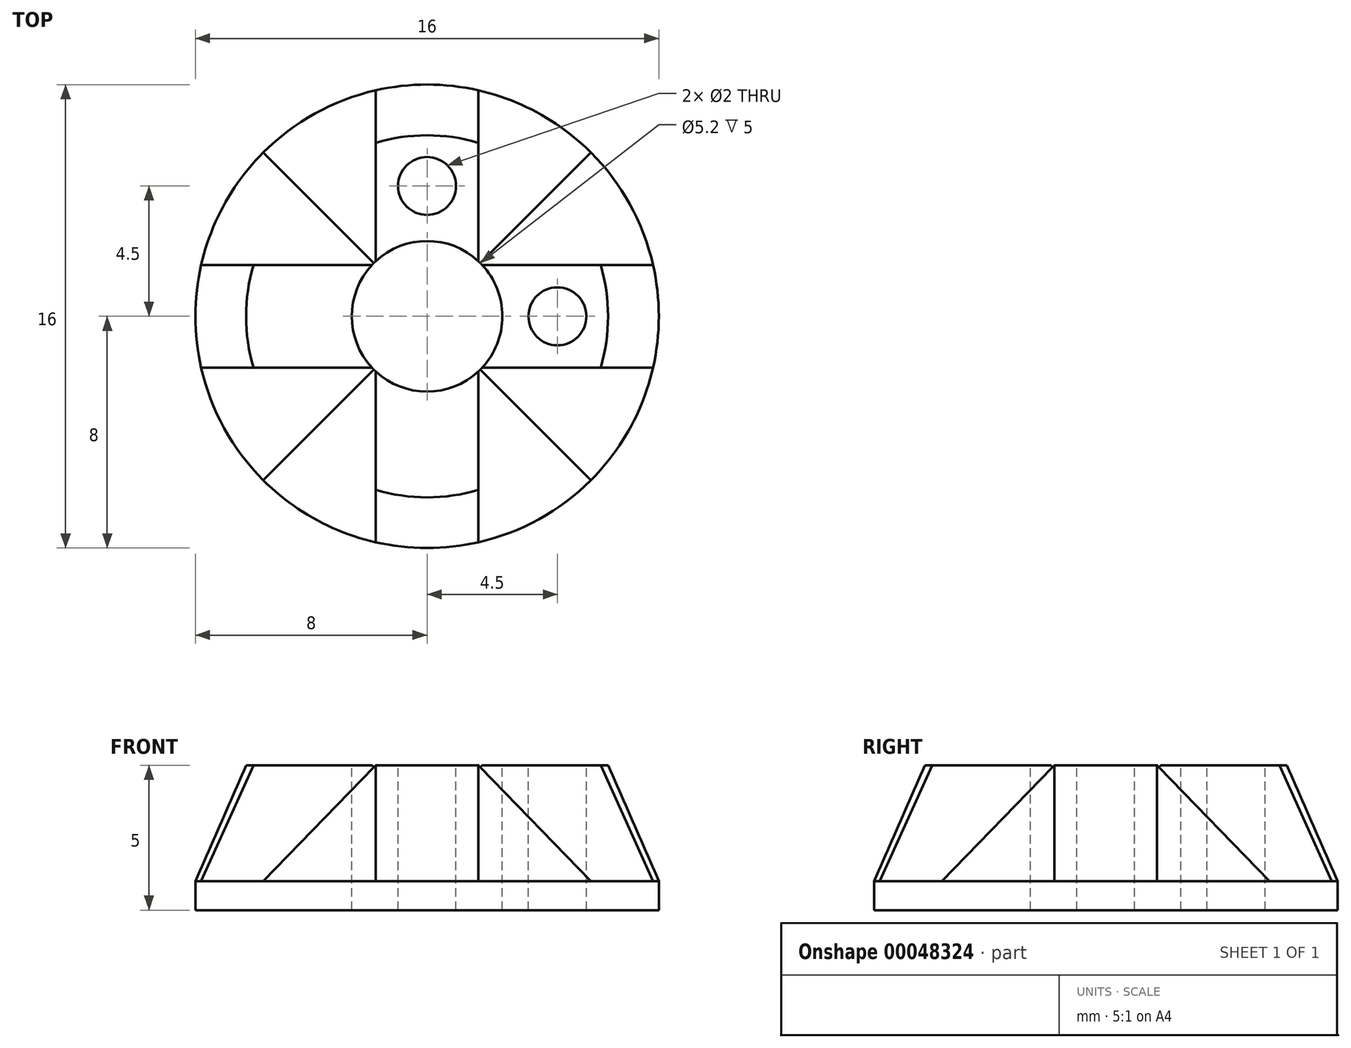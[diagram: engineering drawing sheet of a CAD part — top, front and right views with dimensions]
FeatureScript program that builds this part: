
annotation { "Feature Type Name" : "Feature", "Feature Type Description" : "" }
export const myFeature = defineFeature(function(context is Context, id is Id, definition is map)
    precondition{}
    {
        {
            var Q0;
            Q0=qCreatedBy(makeId("Top.planeOp"),FACE);
            var sketch = newSketch(context, id + "F0", { "sketchPlane" : qUnion([Q0])});
            skLineSegment(sketch, "E0", {"start": v(0, 0) * mm, "end": v(0, 6.25) * mm, "construction": true});
            skLineSegment(sketch, "E1", {"start": v(0, 6.25) * mm, "end": v(1.77, 6.25) * mm, "construction": true});
            skLineSegment(sketch, "E2.left", {"start": v(1.77, 6) * mm, "end": v(1.77, 1.78) * mm});
            skLineSegment(sketch, "E2.right", {"start": v(-1.78, 6) * mm, "end": v(-1.78, 1.77) * mm});
            skLineSegment(sketch, "E3", {"start": v(0, 0) * mm, "end": v(6.63, 6.63) * mm, "construction": true});
            skLineSegment(sketch, "E4.MirrorCS", {"start": v(6, 1.78) * mm, "end": v(1.78, 1.78) * mm});
            skLineSegment(sketch, "E5.MirrorCS", {"start": v(6, -1.78) * mm, "end": v(1.78, -1.78) * mm});
            skLineSegment(sketch, "E6", {"start": v(0, 0) * mm, "end": v(0, 4.5) * mm, "construction": true});
            skLineSegment(sketch, "E7", {"start": v(0, 4.5) * mm, "end": v(0, -4.5) * mm, "construction": true});
            skPoint(sketch, "E7.endSnap0", {"position": v(0, -1.78) * mm});
            skArc(sketch, "E8", {"start": v(6, -1.77) * mm, "mid": v(6.25, 0) * mm, "end": v(6, 1.78) * mm});
            skPoint(sketch, "E9.orphan", {"position": v(-1.78, 6.25) * mm});
            skPoint(sketch, "E10.orphan", {"position": v(6.25, 1.78) * mm});
            skPoint(sketch, "E11.MirrorCS.end.orphan", {"position": v(6.25, -1.78) * mm});
            skPoint(sketch, "E12.orphan", {"position": v(1.77, -6.25) * mm});
            skPoint(sketch, "E13.orphan", {"position": v(-6.25, -1.78) * mm});
            skPoint(sketch, "E14.MirrorCS.start.orphan", {"position": v(-6.25, 1.78) * mm});
            skPoint(sketch, "E15.orphan", {"position": v(-6.25, 1.77) * mm});
            skArc(sketch, "E16.trimOffspring", {"start": v(-1.77, -6) * mm, "mid": v(0, -6.25) * mm, "end": v(1.77, -6) * mm});
            skArc(sketch, "E17.trimOffspring", {"start": v(-6, 1.77) * mm, "mid": v(-6.25, 0) * mm, "end": v(-6, -1.77) * mm});
            skArc(sketch, "E18.trimOffspring", {"start": v(1.78, 6) * mm, "mid": v(0, 6.25) * mm, "end": v(-1.78, 6) * mm});
            skPoint(sketch, "E19.orphan", {"position": v(-1.77, -6.25) * mm});
            skLineSegment(sketch, "E20.trimOffspring", {"start": v(-1.78, -1.78) * mm, "end": v(-1.77, -6) * mm});
            skLineSegment(sketch, "E21.trimOffspring", {"start": v(-1.78, -1.78) * mm, "end": v(-6, -1.78) * mm});
            skLineSegment(sketch, "E22.trimOffspring", {"start": v(-1.78, 1.77) * mm, "end": v(-6, 1.77) * mm});
            skLineSegment(sketch, "E23", {"start": v(-1.78, 1.77) * mm, "end": v(1.78, -1.78) * mm});
            skLineSegment(sketch, "E24", {"start": v(1.78, 1.78) * mm, "end": v(-1.78, -1.78) * mm});
            skLineSegment(sketch, "E25.trimOffspring", {"start": v(1.77, -1.78) * mm, "end": v(1.77, -6) * mm});
            skSolve(sketch);
        }
        {
            var Q0;
            Q0=qCreatedBy(makeId("Top.planeOp"),FACE);
            cPlane(context, id + "F1", {"entities" : qUnion([Q0]), "cplaneType" : CPlaneType.OFFSET, "offset" : 5 * mm, "oppositeDirection" : true, "width" : 150 * mm, "height" : 150 * mm});
        }
        {
            var Q0;
            Q0=qCreatedBy(id+"F1.planeOp",FACE);
            var sketch = newSketch(context, id + "F2", { "sketchPlane" : qUnion([Q0])});
            skPoint(sketch, "E26.0", {"position": v(0, 0) * mm});
            skCircle(sketch, "E27", {"center": v(0, 0) * mm, "radius": 8 * mm});
            skSolve(sketch);
        }
        {
            var Q0;
            Q0 = qSketchRegion(id + "F2", true);
            extrude(context, id + "F3", {"entities" : qUnion([Q0]), "depth" : 1 * mm});
        }
        {
            var Q0;
            Q0=makeQuery(id+"F3.opExtrude","CAP_FACE",FACE,{"disambiguationData":[OSD([sQuery(id+"F2.wireOp",EDGE,"E27")])],"isStart":false});
            var sketch = newSketch(context, id + "F4", { "sketchPlane" : qUnion([Q0])});
            skPoint(sketch, "E28.0", {"position": v(0, 0) * mm});
            skLineSegment(sketch, "E29", {"start": v(0, 0) * mm, "end": v(0, -8) * mm, "construction": true});
            skLineSegment(sketch, "E30", {"start": v(5.66, 5.66) * mm, "end": v(-5.66, -5.66) * mm});
            skLineSegment(sketch, "E31", {"start": v(-5.66, 5.66) * mm, "end": v(5.66, -5.66) * mm});
            skLineSegment(sketch, "E32.0", {"start": v(-1.78, -1.78) * mm, "end": v(-7.8, -1.78) * mm, "construction": true});
            skLineSegment(sketch, "E33.0", {"start": v(-1.78, 1.77) * mm, "end": v(-7.8, 1.77) * mm, "construction": true});
            skLineSegment(sketch, "E34.0", {"start": v(-1.78, 7.8) * mm, "end": v(-1.78, 1.77) * mm, "construction": true});
            skLineSegment(sketch, "E35.0", {"start": v(7.8, 1.78) * mm, "end": v(1.78, 1.78) * mm, "construction": true});
            skLineSegment(sketch, "E36.0", {"start": v(7.8, -1.78) * mm, "end": v(1.78, -1.78) * mm, "construction": true});
            skPoint(sketch, "E37.orphan", {"position": v(-6, -1.78) * mm});
            skPoint(sketch, "E38.orphan", {"position": v(-6, 1.77) * mm});
            skPoint(sketch, "E39.orphan", {"position": v(-1.78, 6) * mm});
            skLineSegment(sketch, "E40.0", {"start": v(1.77, 7.8) * mm, "end": v(1.77, 1.78) * mm, "construction": true});
            skLineSegment(sketch, "E41.0", {"start": v(1.77, -1.78) * mm, "end": v(1.77, -7.8) * mm, "construction": true});
            skLineSegment(sketch, "E42.0", {"start": v(-1.78, -1.78) * mm, "end": v(-1.77, -7.8) * mm, "construction": true});
            skPoint(sketch, "E43.orphan", {"position": v(-1.77, -6) * mm});
            skPoint(sketch, "E44.orphan", {"position": v(1.77, -6) * mm});
            skPoint(sketch, "E45.orphan", {"position": v(6, -1.78) * mm});
            skPoint(sketch, "E46.orphan", {"position": v(6, 1.78) * mm});
            skPoint(sketch, "E47.orphan", {"position": v(1.77, 6) * mm});
            skPoint(sketch, "E48", {"position": v(-7.8, 1.77) * mm});
            skPoint(sketch, "E49", {"position": v(-7.8, -1.78) * mm});
            skPoint(sketch, "E50", {"position": v(-1.78, 7.8) * mm});
            skPoint(sketch, "E51", {"position": v(1.77, 7.8) * mm});
            skPoint(sketch, "E52", {"position": v(7.8, 1.78) * mm});
            skPoint(sketch, "E53", {"position": v(7.8, -1.78) * mm});
            skPoint(sketch, "E54", {"position": v(1.77, -7.8) * mm});
            skPoint(sketch, "E55", {"position": v(-1.77, -7.8) * mm});
            skArc(sketch, "E56", {"start": v(1.77, 7.8) * mm, "mid": v(0, 8) * mm, "end": v(-1.78, 7.8) * mm});
            skLineSegment(sketch, "E57", {"start": v(-1.78, 7.8) * mm, "end": v(-1.78, 7.8) * mm});
            skArc(sketch, "E58", {"start": v(-1.78, 7.8) * mm, "mid": v(-3.87, 7) * mm, "end": v(-5.66, 5.66) * mm});
            skArc(sketch, "E59", {"start": v(-5.66, 5.66) * mm, "mid": v(-7, 3.87) * mm, "end": v(-7.8, 1.77) * mm});
            skArc(sketch, "E60", {"start": v(5.66, 5.66) * mm, "mid": v(3.87, 7) * mm, "end": v(1.77, 7.8) * mm});
            skLineSegment(sketch, "E61", {"start": v(1.77, 7.8) * mm, "end": v(1.77, 7.8) * mm});
            skArc(sketch, "E62", {"start": v(-7.8, 1.77) * mm, "mid": v(-8, 0) * mm, "end": v(-7.8, -1.78) * mm});
            skArc(sketch, "E63", {"start": v(-7.8, -1.78) * mm, "mid": v(-7, -3.87) * mm, "end": v(-5.66, -5.66) * mm});
            skArc(sketch, "E64", {"start": v(-5.66, -5.66) * mm, "mid": v(-3.87, -7) * mm, "end": v(-1.77, -7.8) * mm});
            skArc(sketch, "E65", {"start": v(-1.77, -7.8) * mm, "mid": v(0, -8) * mm, "end": v(1.77, -7.8) * mm});
            skArc(sketch, "E66", {"start": v(1.77, -7.8) * mm, "mid": v(3.87, -7) * mm, "end": v(5.66, -5.66) * mm});
            skArc(sketch, "E67", {"start": v(5.66, -5.66) * mm, "mid": v(7, -3.87) * mm, "end": v(7.8, -1.77) * mm});
            skArc(sketch, "E68", {"start": v(7.8, -1.78) * mm, "mid": v(8, 0) * mm, "end": v(7.8, 1.78) * mm});
            skArc(sketch, "E69", {"start": v(7.8, 1.78) * mm, "mid": v(7, 3.87) * mm, "end": v(5.66, 5.66) * mm});
            skSolve(sketch);
        }
        {
            var Q1;
            Q1=makeQuery(id+"F4.imprint","IMPRINT",FACE,{"disambiguationData":[TD([[makeQuery(id+"F4.imprint","IMPRINT",EDGE,{"derivedFrom":sQuery(id+"F4.wireOp",EDGE,"E56")}),1.0]])]});
            var Q2;
            {var subQ3=sQuery(id+"F0.wireOp",EDGE,"E2.left");Q2=makeQuery(id+"F0.imprint","IMPRINT",FACE,{"disambiguationData":[TD([[makeQuery(id+"F0.imprint","IMPRINT",EDGE,{"derivedFrom":subQ3}),-1.0]])]});}
            loft(context, id + "F5", {"operationType" : NewBodyOperationType.ADD, "sheetProfilesArray" : [{ "sheetProfileEntities" : qUnion([Q1]) }, { "sheetProfileEntities" : qUnion([Q2]) }]});
        }
        {
            var Q1;
            {var subQ4=sQuery(id+"F4.wireOp",EDGE,"E59");Q1=makeQuery(id+"F4.imprint","IMPRINT",FACE,{"disambiguationData":[TD([[makeQuery(id+"F4.imprint","IMPRINT",EDGE,{"derivedFrom":subQ4}),1.0]])]});}
            var Q2;
            Q2=makeQuery(id+"F0.imprint","IMPRINT",FACE,{"disambiguationData":[TD([[makeQuery(id+"F0.imprint","IMPRINT",EDGE,{"derivedFrom":sQuery(id+"F0.wireOp",EDGE,"E17.trimOffspring")}),1.0]])]});
            loft(context, id + "F6", {"operationType" : NewBodyOperationType.ADD, "sheetProfilesArray" : [{ "sheetProfileEntities" : qUnion([Q1]) }, { "sheetProfileEntities" : qUnion([Q2]) }]});
        }
        {
            var Q1;
            {var subQ4=sQuery(id+"F4.wireOp",EDGE,"E64");Q1=makeQuery(id+"F4.imprint","IMPRINT",FACE,{"disambiguationData":[TD([[makeQuery(id+"F4.imprint","IMPRINT",EDGE,{"derivedFrom":subQ4}),1.0]])]});}
            var Q2;
            Q2=makeQuery(id+"F0.imprint","IMPRINT",FACE,{"disambiguationData":[TD([[makeQuery(id+"F0.imprint","IMPRINT",EDGE,{"derivedFrom":sQuery(id+"F0.wireOp",EDGE,"E16.trimOffspring")}),1.0]])]});
            loft(context, id + "F7", {"operationType" : NewBodyOperationType.ADD, "sheetProfilesArray" : [{ "sheetProfileEntities" : qUnion([Q1]) }, { "sheetProfileEntities" : qUnion([Q2]) }]});
        }
        {
            var Q1;
            {var subQ4=sQuery(id+"F4.wireOp",EDGE,"E67");Q1=makeQuery(id+"F4.imprint","IMPRINT",FACE,{"disambiguationData":[TD([[makeQuery(id+"F4.imprint","IMPRINT",EDGE,{"derivedFrom":subQ4}),1.0]])]});}
            var Q2;
            {var subQ3=sQuery(id+"F0.wireOp",EDGE,"E4.MirrorCS");Q2=makeQuery(id+"F0.imprint","IMPRINT",FACE,{"disambiguationData":[TD([[makeQuery(id+"F0.imprint","IMPRINT",EDGE,{"derivedFrom":subQ3}),1.0]])]});}
            loft(context, id + "F8", {"operationType" : NewBodyOperationType.ADD, "sheetProfilesArray" : [{ "sheetProfileEntities" : qUnion([Q1]) }, { "sheetProfileEntities" : qUnion([Q2]) }]});
        }
        {
            var Q0;
            Q0=qCreatedBy(makeId("Top.planeOp"),FACE);
            var sketch = newSketch(context, id + "F9", { "sketchPlane" : qUnion([Q0])});
            skLineSegment(sketch, "E70", {"start": v(0, 0) * mm, "end": v(0, 4.5) * mm, "construction": true});
            skLineSegment(sketch, "E71", {"start": v(0, 0) * mm, "end": v(4.5, 0) * mm, "construction": true});
            skLineSegment(sketch, "E72", {"start": v(0, -4.5) * mm, "end": v(0, 0) * mm, "construction": true});
            skLineSegment(sketch, "E73", {"start": v(-4.5, 0) * mm, "end": v(0, 0) * mm, "construction": true});
            skCircle(sketch, "E74", {"center": v(4.5, 0) * mm, "radius": 1 * mm});
            skCircle(sketch, "E75", {"center": v(0, 4.5) * mm, "radius": 1 * mm});
            skCircle(sketch, "E76.MirrorC", {"center": v(-4.5, 0) * mm, "radius": 1 * mm});
            skCircle(sketch, "E77.MirrorC", {"center": v(0, -4.5) * mm, "radius": 1 * mm});
            skCircle(sketch, "E78", {"center": v(0, 0) * mm, "radius": 2.6 * mm});
            skSolve(sketch);
        }
        {
            var Q0;
            Q0=makeQuery(id+"F9.imprint","IMPRINT",FACE,{"disambiguationData":[TD([[makeQuery(id+"F9.imprint","IMPRINT",EDGE,{"derivedFrom":sQuery(id+"F9.wireOp",EDGE,"E75")}),1.0]])]});
            var Q1;
            Q1=makeQuery(id+"F9.imprint","IMPRINT",FACE,{"disambiguationData":[TD([[makeQuery(id+"F9.imprint","IMPRINT",EDGE,{"derivedFrom":sQuery(id+"F9.wireOp",EDGE,"E74")}),1.0]])]});
            var Q2;
            Q2=makeQuery(id+"F9.imprint","IMPRINT",FACE,{"disambiguationData":[TD([[makeQuery(id+"F9.imprint","IMPRINT",EDGE,{"derivedFrom":sQuery(id+"F9.wireOp",EDGE,"E77.MirrorC")}),-1.0]])]});
            var Q3;
            Q3=makeQuery(id+"F9.imprint","IMPRINT",FACE,{"disambiguationData":[TD([[makeQuery(id+"F9.imprint","IMPRINT",EDGE,{"derivedFrom":sQuery(id+"F9.wireOp",EDGE,"E76.MirrorC")}),-1.0]])]});
            var Q4;
            Q4=makeQuery(id+"F9.imprint","IMPRINT",FACE,{"disambiguationData":[TD([[makeQuery(id+"F9.imprint","IMPRINT",EDGE,{"derivedFrom":sQuery(id+"F9.wireOp",EDGE,"E78")}),1.0]])]});
            extrude(context, id + "F10", {"entities" : qUnion([Q0, Q1, Q2, Q3, Q4]), "operationType" : NewBodyOperationType.REMOVE, "endBound" : BoundingType.THROUGH_ALL, "oppositeDirection" : true, "depth" : 21 * mm});
        }
    });
